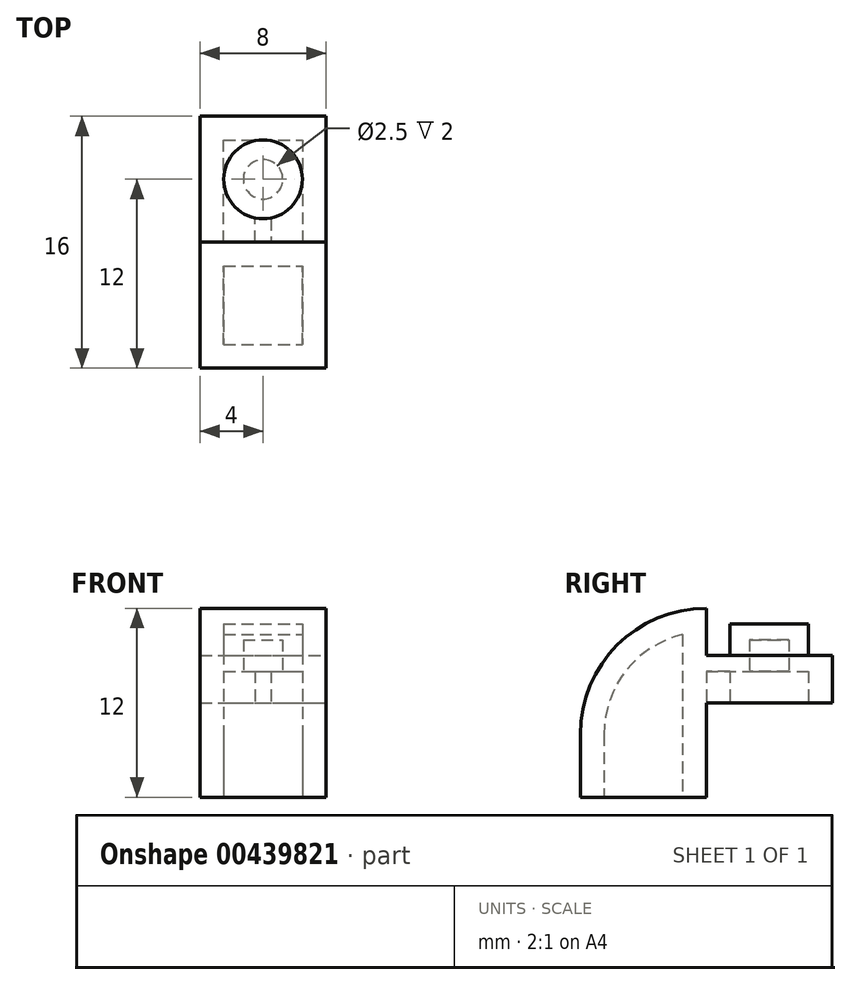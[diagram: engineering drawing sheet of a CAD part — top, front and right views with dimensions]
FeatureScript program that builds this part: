
annotation { "Feature Type Name" : "Feature", "Feature Type Description" : "" }
export const myFeature = defineFeature(function(context is Context, id is Id, definition is map)
    precondition{}
    {
        {
            var Q0;
            Q0=qCreatedBy(makeId("Right.planeOp"),FACE);
            var sketch = newSketch(context, id + "F0", { "sketchPlane" : qUnion([Q0])});
            skLineSegment(sketch, "E0.bottom", {"start": v(0, 0) * mm, "end": v(8, 0) * mm});
            skLineSegment(sketch, "E0.top", {"start": v(8, 12) * mm, "end": v(8, 12) * mm});
            skLineSegment(sketch, "E0.left", {"start": v(0, 0) * mm, "end": v(0, 4) * mm});
            skLineSegment(sketch, "E0.right", {"start": v(16, 6) * mm, "end": v(16, 9) * mm});
            skLineSegment(sketch, "E1", {"start": v(16, 6) * mm, "end": v(8, 6) * mm});
            skLineSegment(sketch, "E2", {"start": v(8, 6) * mm, "end": v(8, 0) * mm});
            skPoint(sketch, "E3.orphan", {"position": v(16, 0) * mm});
            skLineSegment(sketch, "E4", {"start": v(8, 12) * mm, "end": v(8, 9) * mm});
            skLineSegment(sketch, "E5", {"start": v(8, 9) * mm, "end": v(16, 9) * mm});
            skPoint(sketch, "E6.orphan", {"position": v(16, 12) * mm});
            skPoint(sketch, "E7.visualSharp", {"position": v(0, 12) * mm});
            skArc(sketch, "E7.filletArc", {"start": v(8, 12) * mm, "mid": v(2.34, 9.66) * mm, "end": v(0, 4) * mm});
            skSolve(sketch);
        }
        {
            var Q0;
            Q0 = qSketchRegion(id + "F0", true);
            extrude(context, id + "F1", {"entities" : qUnion([Q0]), "oppositeDirection" : true, "depth" : 4 * mm});
        }
        {
            var Q0;
            Q0=makeQuery(id+"F1.opExtrude","CAP_FACE",FACE,{"disambiguationData":[OSD([sQuery(id+"F0.wireOp",EDGE,"E0.bottom"),sQuery(id+"F0.wireOp",EDGE,"E0.left"),sQuery(id+"F0.wireOp",EDGE,"E0.right"),sQuery(id+"F0.wireOp",EDGE,"E1"),sQuery(id+"F0.wireOp",EDGE,"E2"),sQuery(id+"F0.wireOp",EDGE,"E4"),sQuery(id+"F0.wireOp",EDGE,"E5"),sQuery(id+"F0.wireOp",EDGE,"E7.filletArc")])],"isStart":true});
            var sketch = newSketch(context, id + "F2", { "sketchPlane" : qUnion([Q0])});
            skArc(sketch, "E8.0", {"start": v(6.5, 10.32) * mm, "mid": v(2.9, 8.03) * mm, "end": v(1.5, 4) * mm});
            skLineSegment(sketch, "E9", {"start": v(6.5, 10.32) * mm, "end": v(6.5, 0) * mm});
            skLineSegment(sketch, "E10", {"start": v(1.5, 4) * mm, "end": v(1.5, 0) * mm});
            skLineSegment(sketch, "E11", {"start": v(1.5, 0) * mm, "end": v(6.5, 0) * mm});
            skSolve(sketch);
        }
        {
            var Q0;
            Q0 = qSketchRegion(id + "F2", true);
            extrude(context, id + "F3", {"entities" : qUnion([Q0]), "operationType" : NewBodyOperationType.REMOVE, "oppositeDirection" : true, "depth" : 2.5 * mm});
        }
        {
            var Q0;
            Q0=makeQuery(id+"F1.opExtrude","SWEPT_BODY",BODY,{"disambiguationData":[OSD([sQuery(id+"F0.wireOp",EDGE,"E0.bottom"),sQuery(id+"F0.wireOp",EDGE,"E0.left"),sQuery(id+"F0.wireOp",EDGE,"E0.right"),sQuery(id+"F0.wireOp",EDGE,"E1"),sQuery(id+"F0.wireOp",EDGE,"E2"),sQuery(id+"F0.wireOp",EDGE,"E4"),sQuery(id+"F0.wireOp",EDGE,"E5"),sQuery(id+"F0.wireOp",EDGE,"E7.filletArc")])]});
            var Q1;
            Q1=makeQuery(id+"F1.opExtrude","CAP_FACE",FACE,{"disambiguationData":[OSD([sQuery(id+"F0.wireOp",EDGE,"E0.bottom"),sQuery(id+"F0.wireOp",EDGE,"E0.left"),sQuery(id+"F0.wireOp",EDGE,"E0.right"),sQuery(id+"F0.wireOp",EDGE,"E1"),sQuery(id+"F0.wireOp",EDGE,"E2"),sQuery(id+"F0.wireOp",EDGE,"E4"),sQuery(id+"F0.wireOp",EDGE,"E5"),sQuery(id+"F0.wireOp",EDGE,"E7.filletArc")])],"isStart":true});
            mirror(context, id + "F4", {"operationType" : NewBodyOperationType.ADD, "entities" : qUnion([Q0]), "mirrorPlane" : qUnion([Q1])});
        }
        {
            var Q0;
            {var subQ0=makeQuery(id+"F1.opExtrude","SWEPT_FACE",FACE,{"disambiguationData":[OSD([sQuery(id+"F0.wireOp",EDGE,"E5")])]});Q0=makeQuery(id+"F4.boolean.opBoolean","MERGE",FACE,{"derivedFrom":[subQ0,makeQuery(id+"F4.opPattern","COPY",FACE,{"derivedFrom":subQ0,"instanceName":"1"})]});}
            var sketch = newSketch(context, id + "F5", { "sketchPlane" : qUnion([Q0])});
            skCircle(sketch, "E12", {"center": v(0, 12) * mm, "radius": 2.5 * mm});
            skSolve(sketch);
        }
        {
            var Q0;
            Q0 = qSketchRegion(id + "F5", true);
            extrude(context, id + "F6", {"entities" : qUnion([Q0]), "operationType" : NewBodyOperationType.ADD, "depth" : 2 * mm});
        }
        {
            var Q0;
            {var subQ0=makeQuery(id+"F1.opExtrude","SWEPT_FACE",FACE,{"disambiguationData":[OSD([sQuery(id+"F0.wireOp",EDGE,"E1")])]});Q0=makeQuery(id+"F4.boolean.opBoolean","MERGE",FACE,{"derivedFrom":[subQ0,makeQuery(id+"F4.opPattern","COPY",FACE,{"derivedFrom":subQ0,"instanceName":"1"})]});}
            var sketch = newSketch(context, id + "F7", { "sketchPlane" : qUnion([Q0])});
            skCircle(sketch, "E13", {"center": v(0, -12) * mm, "radius": 1.25 * mm});
            skSolve(sketch);
        }
        {
            var Q0;
            Q0=makeQuery(id+"F7.imprint","IMPRINT",FACE,{"disambiguationData":[TD([[makeQuery(id+"F7.imprint","IMPRINT",EDGE,{"derivedFrom":sQuery(id+"F7.wireOp",EDGE,"E13")}),1.0]])]});
            extrude(context, id + "F8", {"entities" : qUnion([Q0]), "operationType" : NewBodyOperationType.REMOVE, "oppositeDirection" : true, "depth" : 4 * mm});
        }
        {
            var Q0;
            {var subQ0=makeQuery(id+"F1.opExtrude","SWEPT_FACE",FACE,{"disambiguationData":[OSD([sQuery(id+"F0.wireOp",EDGE,"E1")])]});Q0=makeQuery(id+"F4.boolean.opBoolean","MERGE",FACE,{"derivedFrom":[subQ0,makeQuery(id+"F4.opPattern","COPY",FACE,{"derivedFrom":subQ0,"instanceName":"1"})]});}
            var sketch = newSketch(context, id + "F9", { "sketchPlane" : qUnion([Q0])});
            skLineSegment(sketch, "E14.0", {"start": v(-2.5, -14.5) * mm, "end": v(2.5, -14.5) * mm});
            skLineSegment(sketch, "E14.1", {"start": v(-2.5, -8) * mm, "end": v(-2.5, -14.5) * mm});
            skLineSegment(sketch, "E14.3", {"start": v(2.5, -14.5) * mm, "end": v(2.5, -8) * mm});
            skLineSegment(sketch, "E15", {"start": v(-2.5, -8) * mm, "end": v(-0.5, -8) * mm});
            skLineSegment(sketch, "E16", {"start": v(-0.5, -8) * mm, "end": v(-0.5, -9.5) * mm});
            skLineSegment(sketch, "E17", {"start": v(-0.5, -9.5) * mm, "end": v(0.5, -9.5) * mm});
            skLineSegment(sketch, "E18", {"start": v(0.5, -9.5) * mm, "end": v(0.5, -8) * mm});
            skLineSegment(sketch, "E19.trimOffspring", {"start": v(0.5, -8) * mm, "end": v(2.5, -8) * mm});
            skSolve(sketch);
        }
        {
            var Q0;
            Q0 = qSketchRegion(id + "F9", true);
            extrude(context, id + "F10", {"entities" : qUnion([Q0]), "operationType" : NewBodyOperationType.REMOVE, "oppositeDirection" : true, "depth" : 2 * mm});
        }
    });
